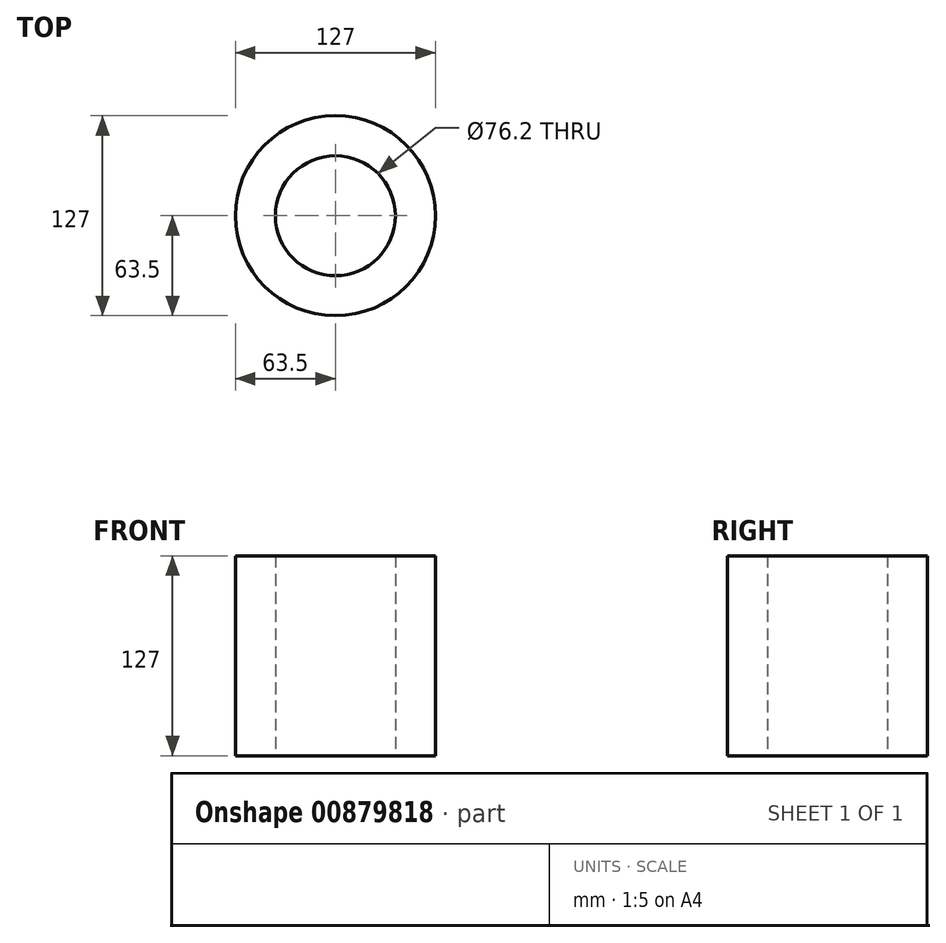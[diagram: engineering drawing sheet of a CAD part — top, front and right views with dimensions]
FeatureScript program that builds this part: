
annotation { "Feature Type Name" : "Feature", "Feature Type Description" : "" }
export const myFeature = defineFeature(function(context is Context, id is Id, definition is map)
    precondition{}
    {
        {
            var Q0;
            Q0=qCreatedBy(makeId("Top.planeOp"),FACE);
            var sketch = newSketch(context, id + "F0", { "sketchPlane" : qUnion([Q0])});
            skCircle(sketch, "E0", {"center": v(0, 0) * mm, "radius": 63.5 * mm});
            skCircle(sketch, "E1", {"center": v(0, 0) * mm, "radius": 38.1 * mm});
            skSolve(sketch);
        }
        {
            var Q0;
            Q0=makeQuery(id+"F0.imprint","IMPRINT",FACE,{"disambiguationData":[TD([[makeQuery(id+"F0.imprint","IMPRINT",EDGE,{"derivedFrom":sQuery(id+"F0.wireOp",EDGE,"E0")}),1.0]])]});
            extrude(context, id + "F1", {"entities" : qUnion([Q0]), "depth" : 127 * mm, "offsetDistance" : 25.4 * mm});
        }
    });
